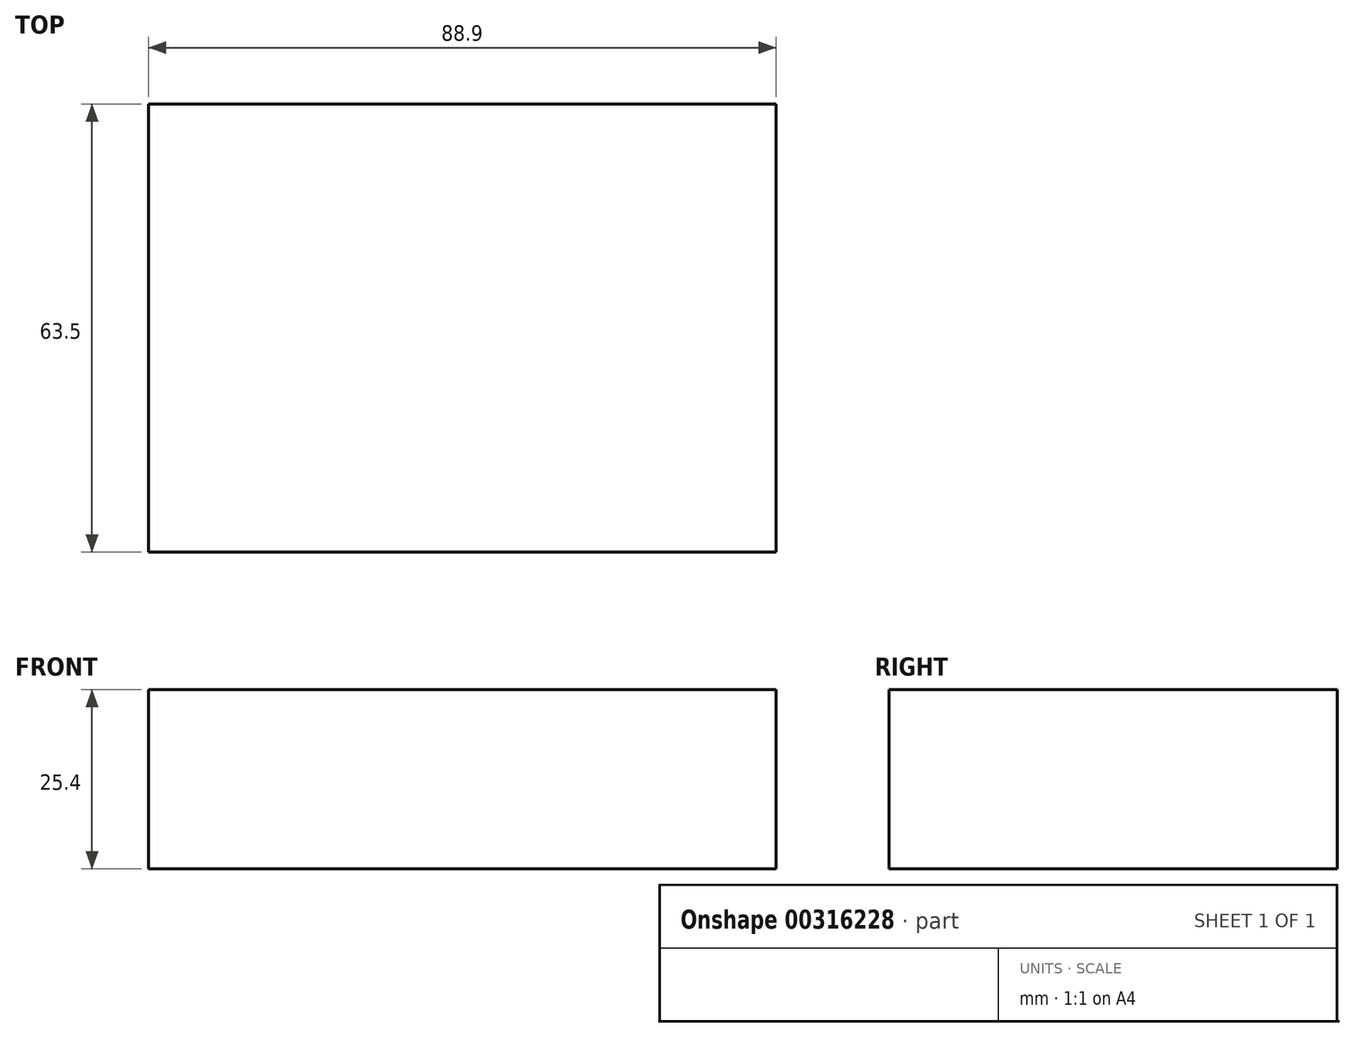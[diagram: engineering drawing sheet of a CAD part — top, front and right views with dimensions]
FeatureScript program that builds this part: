
annotation { "Feature Type Name" : "Feature", "Feature Type Description" : "" }
export const myFeature = defineFeature(function(context is Context, id is Id, definition is map)
    precondition{}
    {
        {
            var Q0;
            Q0=qCreatedBy(makeId("Top.planeOp"),FACE);
            var sketch = newSketch(context, id + "F0", { "sketchPlane" : qUnion([Q0])});
            skLineSegment(sketch, "E0.bottom", {"start": v(-20.15, -31.66) * mm, "end": v(68.75, -31.66) * mm});
            skLineSegment(sketch, "E0.top", {"start": v(-20.15, 31.84) * mm, "end": v(68.75, 31.84) * mm});
            skLineSegment(sketch, "E0.left", {"start": v(-20.15, -31.66) * mm, "end": v(-20.15, 31.84) * mm});
            skLineSegment(sketch, "E0.right", {"start": v(68.75, -31.66) * mm, "end": v(68.75, 31.84) * mm});
            skSolve(sketch);
        }
        {
            var Q0;
            Q0 = qSketchRegion(id + "F0", true);
            extrude(context, id + "F1", {"entities" : qUnion([Q0]), "depth" : 25.4 * mm});
        }
    });
